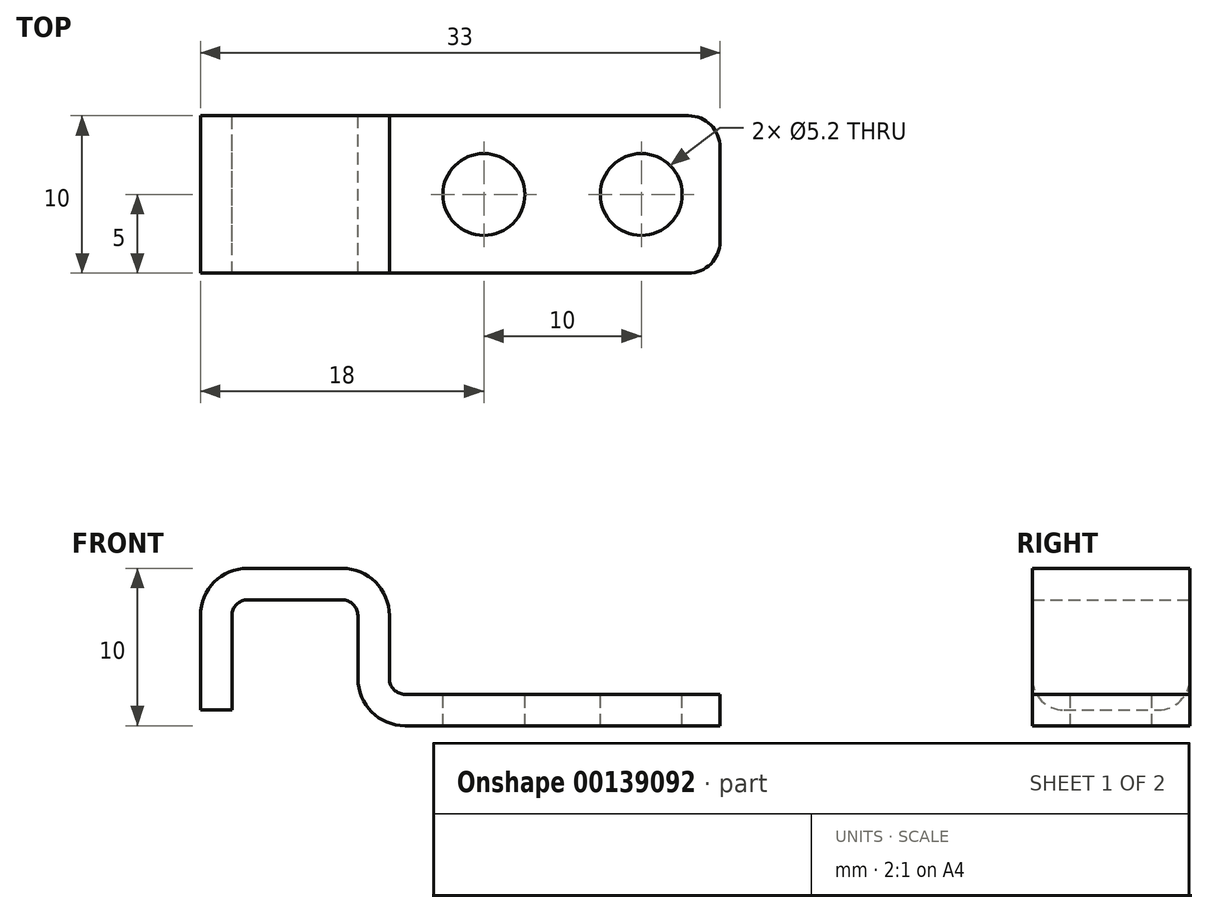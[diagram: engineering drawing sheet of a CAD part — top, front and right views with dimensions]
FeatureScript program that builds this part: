
annotation { "Feature Type Name" : "Feature", "Feature Type Description" : "" }
export const myFeature = defineFeature(function(context is Context, id is Id, definition is map)
    precondition{}
    {
        {
            var Q0;
            Q0=qCreatedBy(makeId("Front.planeOp"),FACE);
            var sketch = newSketch(context, id + "F0", { "sketchPlane" : qUnion([Q0])});
            skLineSegment(sketch, "E0", {"start": v(0, 0) * mm, "end": v(-20, 0) * mm});
            skLineSegment(sketch, "E1", {"start": v(-22, 2) * mm, "end": v(-22, 6) * mm});
            skLineSegment(sketch, "E2", {"start": v(-24, 8) * mm, "end": v(-30, 8) * mm});
            skLineSegment(sketch, "E3", {"start": v(-32, 6) * mm, "end": v(-32, 0) * mm});
            skPoint(sketch, "E4.visualSharp", {"position": v(-22, 8) * mm});
            skArc(sketch, "E4.filletArc", {"start": v(-22, 6) * mm, "mid": v(-22.59, 7.41) * mm, "end": v(-24, 8) * mm});
            skPoint(sketch, "E5.visualSharp", {"position": v(-32, 8) * mm});
            skArc(sketch, "E5.filletArc", {"start": v(-30, 8) * mm, "mid": v(-31.41, 7.41) * mm, "end": v(-32, 6) * mm});
            skPoint(sketch, "E6.visualSharp", {"position": v(-22, 0) * mm});
            skArc(sketch, "E6.filletArc", {"start": v(-22, 2) * mm, "mid": v(-21.41, 0.59) * mm, "end": v(-20, 0) * mm});
            skSolve(sketch);
        }
        {
            var Q0;
            Q0=qCreatedBy(makeId("Right.planeOp"),FACE);
            var sketch = newSketch(context, id + "F1", { "sketchPlane" : qUnion([Q0])});
            skLineSegment(sketch, "E7.bottom", {"start": v(0, -1) * mm, "end": v(10, -1) * mm});
            skLineSegment(sketch, "E7.top", {"start": v(0, 1) * mm, "end": v(10, 1) * mm});
            skLineSegment(sketch, "E7.left", {"start": v(0, -1) * mm, "end": v(0, 1) * mm});
            skLineSegment(sketch, "E7.right", {"start": v(10, -1) * mm, "end": v(10, 1) * mm});
            skSolve(sketch);
        }
        {
            var Q0;
            Q0 = qSketchRegion(id + "F1", true);
            var Q1;
            Q1 = qConstructionFilter(qBodyType(qCreatedBy(id + "F0" ,EDGE), BodyType.WIRE), ConstructionObject.NO);
            sweep(context, id + "F2", {"profiles" : qUnion([Q0]), "path" : qUnion([Q1])});
        }
        {
            var Q0;
            Q0=makeQuery(id+"F2.opSweep","CAP_EDGE",EDGE,{"disambiguationData":[OSD([sQuery(id+"F0.wireOp",VERTEX,"E3.end"),sQuery(id+"F1.wireOp",EDGE,"E7.left")])],"isStart":false});
            var Q1;
            Q1=makeQuery(id+"F2.opSweep","CAP_EDGE",EDGE,{"disambiguationData":[OSD([sQuery(id+"F0.wireOp",VERTEX,"E3.end"),sQuery(id+"F1.wireOp",EDGE,"E7.right")])],"isStart":false});
            fillet(context, id + "F3", {"entities" : qUnion([Q0, Q1]), "radius" : 2 * mm, "tangentPropagation" : true, "allowEdgeOverflow" : false});
        }
        {
            var Q0;
            Q0=makeQuery(id+"F2.opSweep","CAP_EDGE",EDGE,{"disambiguationData":[OSD([sQuery(id+"F0.wireOp",VERTEX,"E0.start"),sQuery(id+"F1.wireOp",EDGE,"E7.left")])],"isStart":true});
            var Q1;
            Q1=makeQuery(id+"F2.opSweep","CAP_EDGE",EDGE,{"disambiguationData":[OSD([sQuery(id+"F0.wireOp",VERTEX,"E0.start"),sQuery(id+"F1.wireOp",EDGE,"E7.right")])],"isStart":true});
            fillet(context, id + "F4", {"entities" : qUnion([Q0, Q1]), "radius" : 2 * mm, "tangentPropagation" : true, "allowEdgeOverflow" : false});
        }
        {
            var Q0;
            Q0=makeQuery(id+"F2.opSweep","SWEPT_FACE",FACE,{"disambiguationData":[OSD([sQuery(id+"F0.wireOp",EDGE,"E0"),sQuery(id+"F1.wireOp",EDGE,"E7.top")])]});
            var sketch = newSketch(context, id + "F5", { "sketchPlane" : qUnion([Q0])});
            skPoint(sketch, "E8", {"position": v(-15, 5) * mm});
            skPoint(sketch, "E9", {"position": v(-5, 5) * mm});
            skSolve(sketch);
        }
        {
            var Q0;
            Q0=sQuery(id+"F5.wireOp",VERTEX,"E8");
            var Q1;
            Q1=sQuery(id+"F5.wireOp",VERTEX,"E9");
            var Q2;
            Q2=makeQuery(id+"F2.opSweep","SWEPT_BODY",BODY,{"disambiguationData":[OSD([sQuery(id+"F0.wireOp",EDGE,"E0"),sQuery(id+"F1.wireOp",EDGE,"E7.bottom"),sQuery(id+"F1.wireOp",EDGE,"E7.top"),sQuery(id+"F1.wireOp",EDGE,"E7.left"),sQuery(id+"F1.wireOp",EDGE,"E7.right")])]});
            hole(context, id + "F6", {"style" : HoleStyle.SIMPLE, "endStyle" : HoleEndStyle.THROUGH, "holeDiameter" : 5.2 * mm, "locations" : qUnion([Q0, Q1]), "scope" : qUnion([Q2]), "isTappedThrough" : true});
        }
    });
